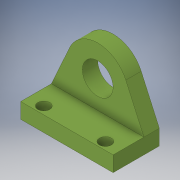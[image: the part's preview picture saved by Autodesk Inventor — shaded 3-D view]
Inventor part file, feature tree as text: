
AUTODESK INVENTOR PART (.ipt)
format: ipt  version: 2018 (Build 220112000, 112)  size: 127,488 bytes
history: native  units: in
note: dims shown in document units (in); Inventor stores cm internally (conversion verified against a paired STEP export)
features: other x3, extrude x2, sketch x2, projected_geometry x1, reference x1
ambient origin geometry x8: Origin, YZ Plane, XZ Plane, XY Plane, X Axis, Y Axis, Z Axis, Center Point
bodies: Solid1 (feature_tree)
feature tree (9):
  extrude  "Extrusion1"  Depth=0.195in
  extrude  "Extrusion2"  Depth=0.25in
  sketch  "Sketch1"  dims[d0=0.195in d1=0.195in]
  sketch  "Sketch2"  dims[d2=1.0in d3=0.25in d4=0.125in d5=0.25in d6=0.75in d7=0.25in d8=0.0in d9=0.25in d10=0.5in d11=0.25in d12=0.0in]
  projected_geometry  "Projected Loop1"
  reference  "Reference1"
  parser-record x1  (decoder bookkeeping rows leaked as tree rows — omitted from the tree; the rows remain in map.json)
  other  "Assembly2.iam"
  other  "0_375_Hex_ID_x_1_125_OD_x_0_313_WD_Flanged_Bearing_217-2735:2"
note: 1 file-system path scrubbed to <path> (originals preserved in map.json)
